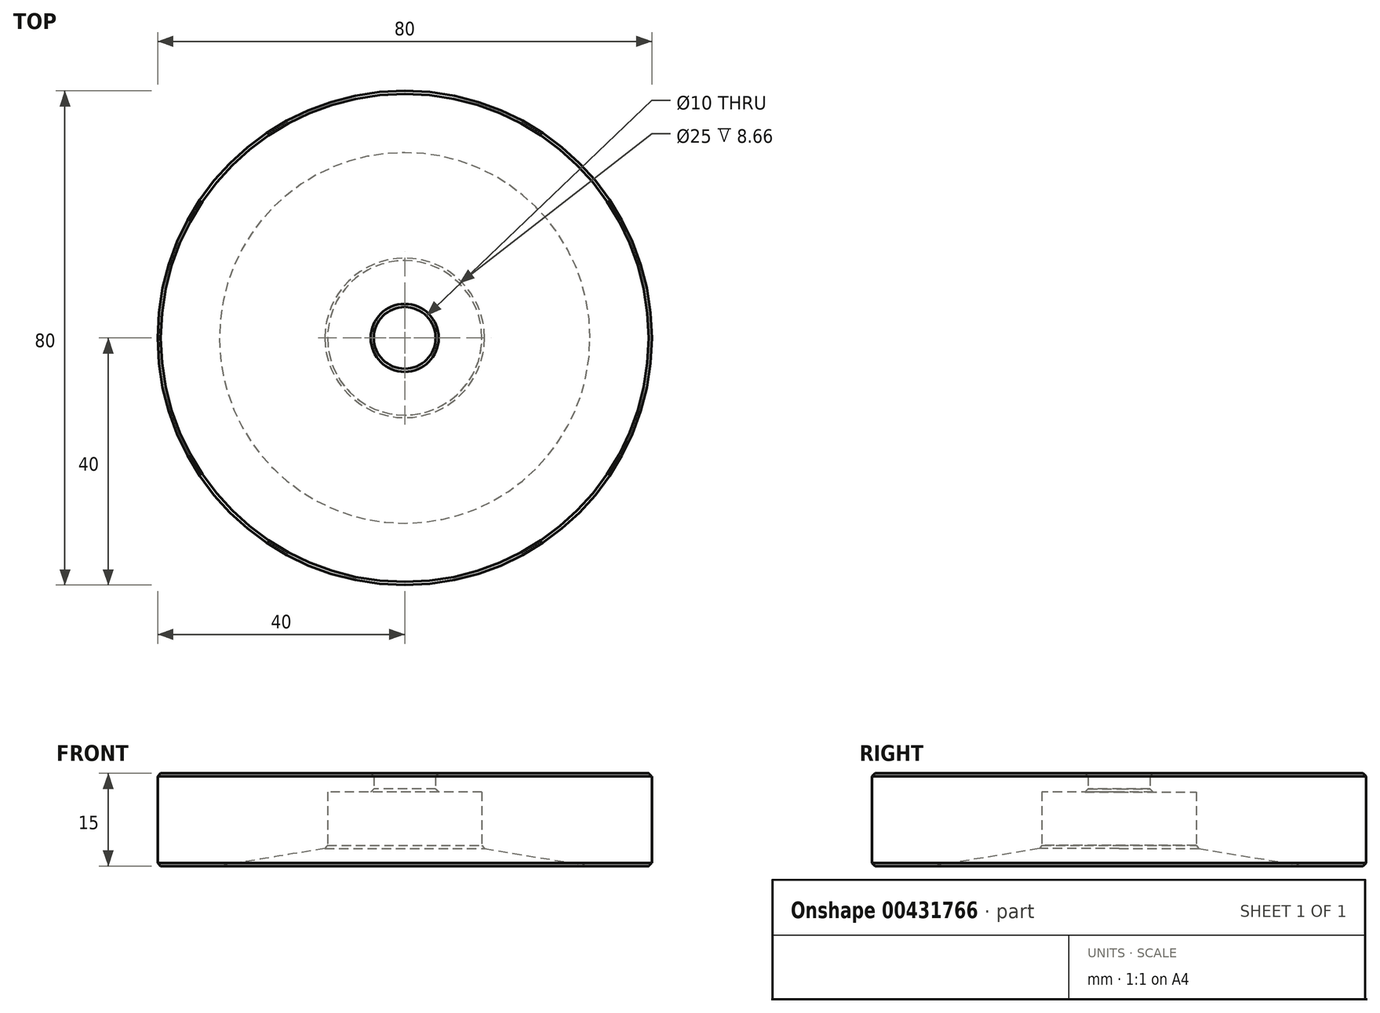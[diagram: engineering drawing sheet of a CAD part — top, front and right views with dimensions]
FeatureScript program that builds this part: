
annotation { "Feature Type Name" : "Feature", "Feature Type Description" : "" }
export const myFeature = defineFeature(function(context is Context, id is Id, definition is map)
    precondition{}
    {
        {
            var Q0;
            Q0=qCreatedBy(makeId("Top.planeOp"),FACE);
            var sketch = newSketch(context, id + "F0", { "sketchPlane" : qUnion([Q0])});
            skCircle(sketch, "E0", {"center": v(0, 0) * mm, "radius": 40 * mm});
            skCircle(sketch, "E1", {"center": v(0, 0) * mm, "radius": 5 * mm});
            skSolve(sketch);
        }
        {
            var Q0;
            Q0=makeQuery(id+"F0.imprint","IMPRINT",FACE,{"disambiguationData":[TD([[makeQuery(id+"F0.imprint","IMPRINT",EDGE,{"derivedFrom":sQuery(id+"F0.wireOp",EDGE,"E0")}),1.0]])]});
            extrude(context, id + "F1", {"entities" : qUnion([Q0]), "depth" : 15 * mm});
        }
        {
            var Q0;
            Q0=qCreatedBy(makeId("Right.planeOp"),FACE);
            var sketch = newSketch(context, id + "F2", { "sketchPlane" : qUnion([Q0])});
            skLineSegment(sketch, "E2", {"start": v(0, 0) * mm, "end": v(0, 5) * mm});
            skLineSegment(sketch, "E3", {"start": v(0, 5) * mm, "end": v(-30, 0) * mm});
            skLineSegment(sketch, "E4", {"start": v(-30, 0) * mm, "end": v(0, 0) * mm});
            skLineSegment(sketch, "E5", {"start": v(0, 0) * mm, "end": v(0, 6.7) * mm, "construction": true});
            skLineSegment(sketch, "E6", {"start": v(0, 0) * mm, "end": v(0, -7.72) * mm, "construction": true});
            skSolve(sketch);
        }
        {
            var Q0;
            Q0=makeQuery(id+"F2.imprint","IMPRINT",FACE,{"disambiguationData":[TD([[makeQuery(id+"F2.imprint","IMPRINT",EDGE,{"derivedFrom":sQuery(id+"F2.wireOp",EDGE,"E2")}),1.0]])]});
            var Q1;
            Q1=sQuery(id+"F2.wireOp",EDGE,"E6");
            revolve(context, id + "F3", {"operationType" : NewBodyOperationType.REMOVE, "entities" : qUnion([Q0]), "axis" : qUnion([Q1]), "revolveType" : RevolveType.FULL, "oppositeDirection" : true});
        }
        {
            var Q0;
            Q0=qCreatedBy(makeId("Top.planeOp"),FACE);
            var sketch = newSketch(context, id + "F4", { "sketchPlane" : qUnion([Q0])});
            skCircle(sketch, "E7", {"center": v(0, 0) * mm, "radius": 12.5 * mm});
            skSolve(sketch);
        }
        {
            var Q0;
            Q0 = qSketchRegion(id + "F4", true);
            extrude(context, id + "F5", {"entities" : qUnion([Q0]), "operationType" : NewBodyOperationType.REMOVE, "depth" : 12 * mm});
        }
        {
            var Q0;
            Q0=makeQuery(id+"F1.opExtrude","CAP_EDGE",EDGE,{"disambiguationData":[OSD([sQuery(id+"F0.wireOp",EDGE,"E0")])],"isStart":false});
            var Q1;
            Q1=makeQuery(id+"F1.opExtrude","CAP_EDGE",EDGE,{"disambiguationData":[OSD([sQuery(id+"F0.wireOp",EDGE,"E0")])],"isStart":true});
            var Q2;
            Q2=makeQuery(id+"F5.boolean.opBoolean","INTERSECT",EDGE,{"derivedFrom":[makeQuery(id+"F3.boolean.opBoolean","COPY",FACE,{"derivedFrom":makeQuery(id+"F3.opRevolve","SWEPT_FACE",FACE,{"disambiguationData":[OSD([sQuery(id+"F2.wireOp",EDGE,"E3")])]})}),makeQuery(id+"F5.opExtrude","SWEPT_FACE",FACE,{"disambiguationData":[OSD([sQuery(id+"F4.wireOp",EDGE,"E7")])]})]});
            var Q3;
            Q3=makeQuery(id+"F5.boolean.opBoolean","INTERSECT",EDGE,{"derivedFrom":[makeQuery(id+"F1.opExtrude","SWEPT_FACE",FACE,{"disambiguationData":[OSD([sQuery(id+"F0.wireOp",EDGE,"E1")])]}),makeQuery(id+"F5.opExtrude","CAP_FACE",FACE,{"disambiguationData":[OSD([sQuery(id+"F4.wireOp",EDGE,"E7")])],"isStart":false})]});
            var Q4;
            Q4=makeQuery(id+"F1.opExtrude","CAP_EDGE",EDGE,{"disambiguationData":[OSD([sQuery(id+"F0.wireOp",EDGE,"E1")])],"isStart":false});
            chamfer(context, id + "F6", {"entities" : qUnion([Q0, Q1, Q2, Q3, Q4]), "width" : 0.5 * mm, "tangentPropagation" : true});
        }
    });
